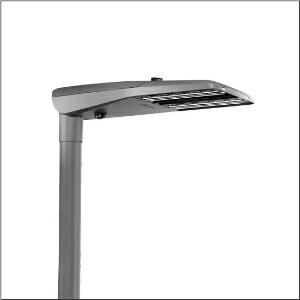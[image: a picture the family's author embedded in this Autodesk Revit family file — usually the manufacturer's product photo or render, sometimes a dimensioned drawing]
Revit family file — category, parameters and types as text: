
# Revit family: streetlight_sl_11_iq_midi___st1_0a_5xc3m51y08me_5fc7
name_source: partatom
category: Lighting Fixtures
units: mm (PartAtom-declared; Revit-internal decimal feet)

## family parameters
Cut with Voids When Loaded = No
Host = Face
Light Source = No
Part Type = Normal
Room Calculation Point = No
Round Connector Dimension = Use Diameter
Shared = No

## types (1)
- --- (1 x LED, 17540 lm, 122.7 W, 3000K)
    Apparent Load = 123 VA
    CIE Flux Codes = 33 66 96 100 100
    Color Rendering = 70
    Color Temperature = 3000K
    Default Elevation = 1800 mm
    Description = Streetlight SL 11 iQ midi, mast luminaire, primary light control with 3 zone facetted reflector, of plastic, silver coated, highly specular, primary optical cover: cover, of PMMA, transparent, light distribution: ST1.0a, light emission: direct distribution, primary light characteristic: asymmetric, installation type: post-top, side-entry, LED, High Power LED, rated luminous flux: 17.540lm, luminous efficacy: 143lm/W, light colour: 730, colour temperature: 3000K, control: presetting dimming logarithmic, Street-Remote, Auto-Match, Temp-Guard, Lumen-Switch, Night-Set, Smart-Wire, Light-Fading, Desk-Remote (wireless, voltage-free reading and setting of iQ features in the workshop via application-optimized NFC function/RFID function), optimised constant luminous flux control (CLO 2.0), with cable H07RN-F 5x 1.5mm², mains connection: 230..240V, AC, 50/60Hz, connection cable pre-assembled, cable length: 12,5m, start of lifetime: 123W, end of service life: 130W, reduction: 56W, luminaire housing, of diecast aluminium, powder-coated, Siteco® metallic grey (DB 702S), please order mast flange separately, inclination adjustable without tools: 0°, 5°, 10°, 15° (post-top) | 0°, -5°, -10°, -15° (side-entry), sealing non-destructively replaceable, multi-level sealing system, length: 780mm, width: 376mm, height: 118mm, mast flange for spigot size: 42mm (side-entry): 5XC10008XM4, 60/48mm (side-entry/post-top): 5XC10108XM2, 76/60mm (side-entry/post-top): 5XC10108XM1, equipment: Power, Smart Interface below and above, protection rating (complete): IP66, insulation class (complete): insulation class II (safety insulation), certification: CE, ENEC, VDE, UKCA, impact resistance: IK09, permissible operating ambient temperature for outdoor applications: -25..+50°C, standard-compliant lighting for roads and squares, Environmental Product Declaration (EPD) tested and certified by an independent institute, packaging unit: 1 piece

Light Distribution: ST1.0a
    Height = 118 mm
    Lamp = 1 x LED
    Lamp Light Flux = 17540 lm
    Lamp Power = 122.7 W
    Lamp count = 1
    Length = 780 mm
    Luminous efficacy = 143 lm/W
    Manufacturer = Siteco
    ModVariant = No
    Model = 5XC3M51Y08ME
    Number of Poles = 1
    OnlyDefault = Yes
    Power Factor = 1
    Product Name = Streetlight SL 11 iQ midi | ST1.0a
    Product group = mast luminaire | pylon top
    ProductGroupID = 6100
    Protection Class = Protection class II
    Protection Degree = IP 66
    RLX_Detail_Level = 1
    RLX_Emergency_Light_Flux = 0 lm
    RLX_Emergency_Type = 0
    RLX_Emergency_Type_DB = No
    RlxData = <blob elided: 69273 chars, md5=4b37daee>
    Socket = socket
    Standby Power = 0 W
    System Light Flux = 17540 lm
    System Power = 123 W
    Type Comments = factory setting: luminous flux: 100 % | dim-lin: 254 | 553 mA
    Type Image = l_1004429.jpg
    URL = http://relux.com
    VarID = @adj_020701
    Voltage = 0 V
    Weight = 0.00 kg
    Width = 376 mm

## geometry (parser evidence)
native form markers: Blend x4, Sweep x10
no freeform markers — native parametric forms only
